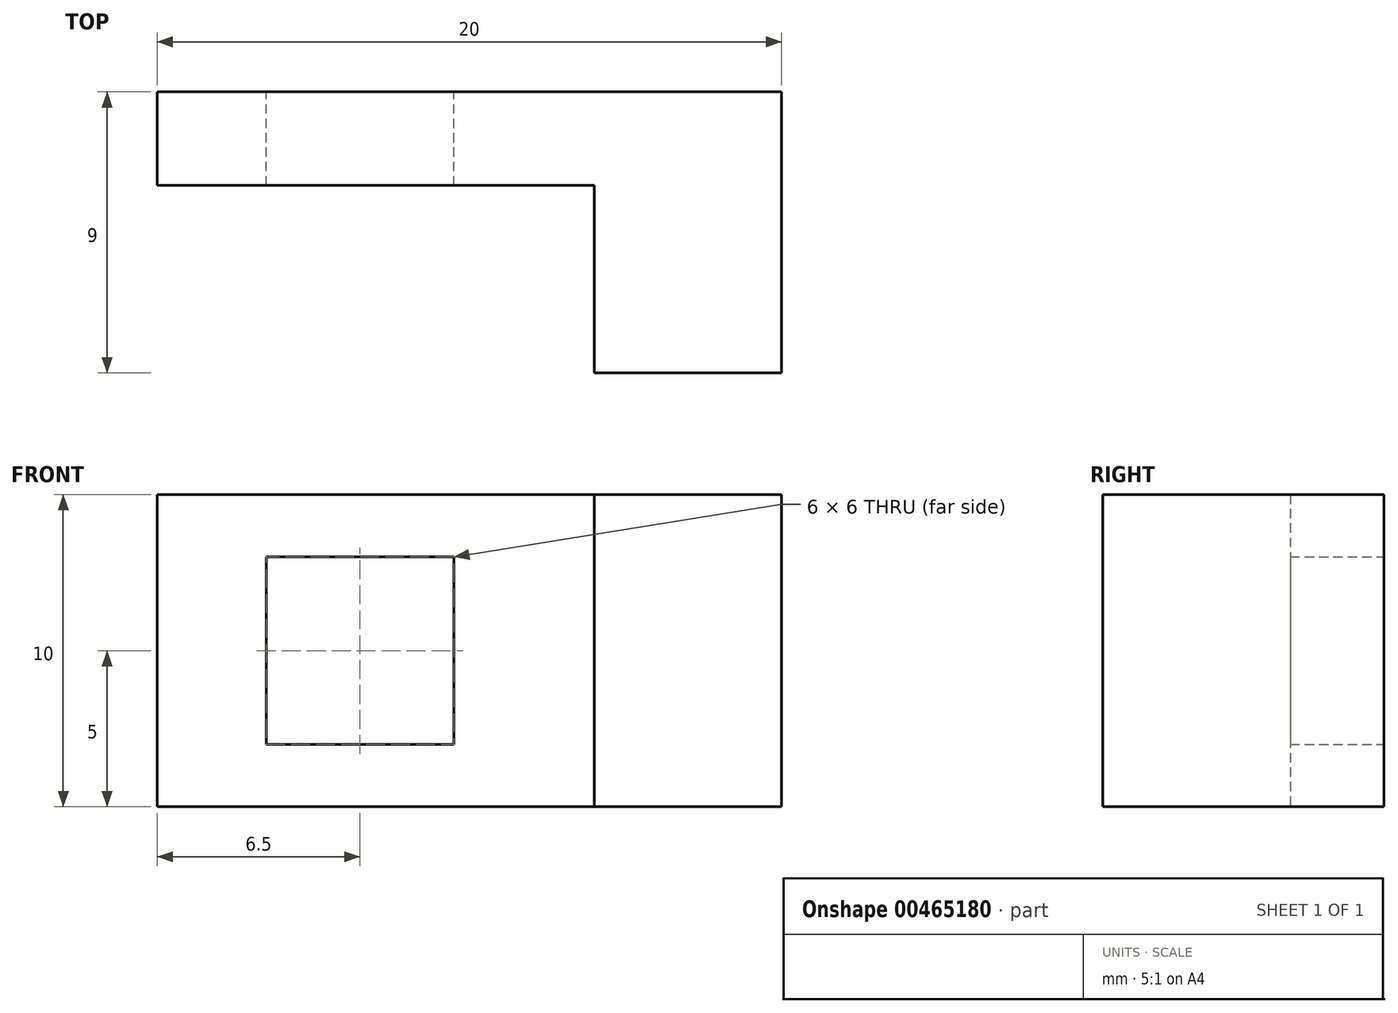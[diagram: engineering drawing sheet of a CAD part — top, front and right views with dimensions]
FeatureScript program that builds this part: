
annotation { "Feature Type Name" : "Feature", "Feature Type Description" : "" }
export const myFeature = defineFeature(function(context is Context, id is Id, definition is map)
    precondition{}
    {
        {
            var Q0;
            Q0=qCreatedBy(makeId("Front.planeOp"),FACE);
            var sketch = newSketch(context, id + "F0", { "sketchPlane" : qUnion([Q0])});
            skLineSegment(sketch, "E0.bottom", {"start": v(10, 5) * mm, "end": v(-10, 5) * mm});
            skLineSegment(sketch, "E0.top", {"start": v(10, -5) * mm, "end": v(-10, -5) * mm});
            skLineSegment(sketch, "E0.left", {"start": v(10, 5) * mm, "end": v(10, -5) * mm});
            skLineSegment(sketch, "E0.right", {"start": v(-10, 5) * mm, "end": v(-10, -5) * mm});
            skPoint(sketch, "E0.middle", {"position": v(0, 0) * mm});
            skLineSegment(sketch, "E1.bottom", {"start": v(-0.5, 3) * mm, "end": v(-6.5, 3) * mm});
            skLineSegment(sketch, "E1.top", {"start": v(-0.5, -3) * mm, "end": v(-6.5, -3) * mm});
            skLineSegment(sketch, "E1.left", {"start": v(-0.5, 3) * mm, "end": v(-0.5, -3) * mm});
            skLineSegment(sketch, "E1.right", {"start": v(-6.5, 3) * mm, "end": v(-6.5, -3) * mm});
            skPoint(sketch, "E1.middle", {"position": v(-3.5, 0) * mm});
            skLineSegment(sketch, "E2", {"start": v(-3.5, 0) * mm, "end": v(0, 0) * mm, "construction": true});
            skLineSegment(sketch, "E3", {"start": v(4, 5) * mm, "end": v(4, -5) * mm});
            skSolve(sketch);
        }
        {
            var Q0;
            {var subQ0=sQuery(id+"F0.wireOp",EDGE,"E0.right");Q0=makeQuery(id+"F0.imprint","IMPRINT",FACE,{"disambiguationData":[TD([[makeQuery(id+"F0.imprint","IMPRINT",EDGE,{"derivedFrom":subQ0}),1.0]])]});}
            extrude(context, id + "F1", {"entities" : qUnion([Q0]), "depth" : 3 * mm});
        }
        {
            var Q0;
            {var subQ0=sQuery(id+"F0.wireOp",EDGE,"E0.left");Q0=makeQuery(id+"F0.imprint","IMPRINT",FACE,{"disambiguationData":[TD([[makeQuery(id+"F0.imprint","IMPRINT",EDGE,{"derivedFrom":subQ0}),-1.0]])]});}
            extrude(context, id + "F2", {"entities" : qUnion([Q0]), "operationType" : NewBodyOperationType.ADD, "depth" : 9 * mm});
        }
    });
